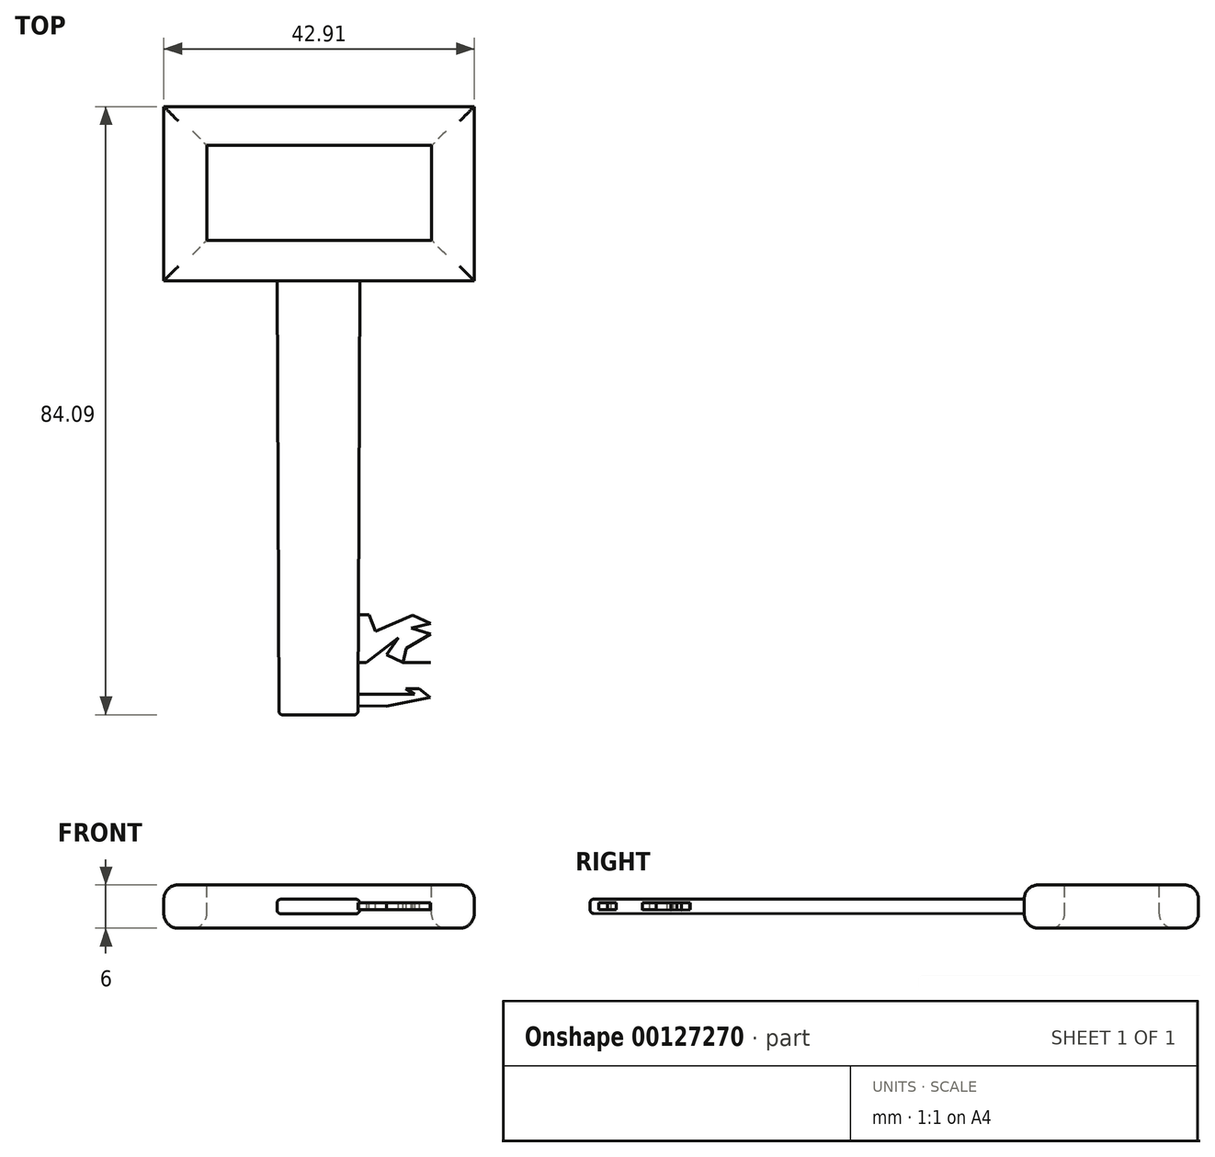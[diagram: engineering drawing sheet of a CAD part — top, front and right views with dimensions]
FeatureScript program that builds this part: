
annotation { "Feature Type Name" : "Feature", "Feature Type Description" : "" }
export const myFeature = defineFeature(function(context is Context, id is Id, definition is map)
    precondition{}
    {
        {
            var Q0;
            Q0=qCreatedBy(makeId("Top.planeOp"),FACE);
            var sketch = newSketch(context, id + "F0", { "sketchPlane" : qUnion([Q0])});
            skLineSegment(sketch, "E0.bottom", {"start": v(-39.45, 64.72) * mm, "end": v(3.46, 64.72) * mm});
            skLineSegment(sketch, "E0.top", {"start": v(-39.45, 40.63) * mm, "end": v(3.46, 40.63) * mm});
            skLineSegment(sketch, "E0.left", {"start": v(-39.45, 64.72) * mm, "end": v(-39.45, 40.63) * mm});
            skLineSegment(sketch, "E0.right", {"start": v(3.46, 64.72) * mm, "end": v(3.46, 40.63) * mm});
            skSolve(sketch);
        }
        {
            var Q0;
            Q0=makeQuery(id+"F0.imprint","IMPRINT",FACE,{"disambiguationData":[TD([[makeQuery(id+"F0.imprint","IMPRINT",EDGE,{"derivedFrom":sQuery(id+"F0.wireOp",EDGE,"E0.bottom")}),-1.0]])]});
            extrude(context, id + "F1", {"entities" : qUnion([Q0]), "depth" : 6 * mm});
        }
        {
            var Q0;
            Q0=makeQuery(id+"F1.opExtrude","CAP_EDGE",EDGE,{"disambiguationData":[OSD([sQuery(id+"F0.wireOp",EDGE,"E0.top")])],"isStart":false});
            var Q1;
            Q1=makeQuery(id+"F1.opExtrude","CAP_EDGE",EDGE,{"disambiguationData":[OSD([sQuery(id+"F0.wireOp",EDGE,"E0.right")])],"isStart":false});
            var Q2;
            Q2=makeQuery(id+"F1.opExtrude","CAP_EDGE",EDGE,{"disambiguationData":[OSD([sQuery(id+"F0.wireOp",EDGE,"E0.bottom")])],"isStart":false});
            var Q3;
            Q3=makeQuery(id+"F1.opExtrude","CAP_EDGE",EDGE,{"disambiguationData":[OSD([sQuery(id+"F0.wireOp",EDGE,"E0.left")])],"isStart":false});
            var Q4;
            Q4=makeQuery(id+"F1.opExtrude","CAP_EDGE",EDGE,{"disambiguationData":[OSD([sQuery(id+"F0.wireOp",EDGE,"E0.top")])],"isStart":true});
            var Q5;
            Q5=makeQuery(id+"F1.opExtrude","CAP_EDGE",EDGE,{"disambiguationData":[OSD([sQuery(id+"F0.wireOp",EDGE,"E0.right")])],"isStart":true});
            var Q6;
            Q6=makeQuery(id+"F1.opExtrude","CAP_EDGE",EDGE,{"disambiguationData":[OSD([sQuery(id+"F0.wireOp",EDGE,"E0.bottom")])],"isStart":true});
            var Q7;
            Q7=makeQuery(id+"F1.opExtrude","CAP_EDGE",EDGE,{"disambiguationData":[OSD([sQuery(id+"F0.wireOp",EDGE,"E0.left")])],"isStart":true});
            fillet(context, id + "F2", {"entities" : qUnion([Q0, Q1, Q2, Q3, Q4, Q5, Q6, Q7]), "radius" : 2 * mm, "tangentPropagation" : true, "allowEdgeOverflow" : false});
        }
        {
            var Q0;
            Q0=makeQuery(id+"F1.opExtrude","CAP_FACE",FACE,{"disambiguationData":[OSD([sQuery(id+"F0.wireOp",EDGE,"E0.bottom"),sQuery(id+"F0.wireOp",EDGE,"E0.top"),sQuery(id+"F0.wireOp",EDGE,"E0.left"),sQuery(id+"F0.wireOp",EDGE,"E0.right")])],"isStart":false});
            var sketch = newSketch(context, id + "F3", { "sketchPlane" : qUnion([Q0])});
            skLineSegment(sketch, "E1.bottom", {"start": v(-33.49, 59.34) * mm, "end": v(-2.43, 59.34) * mm});
            skLineSegment(sketch, "E1.top", {"start": v(-33.49, 46.23) * mm, "end": v(-2.43, 46.23) * mm});
            skLineSegment(sketch, "E1.left", {"start": v(-33.49, 59.34) * mm, "end": v(-33.49, 46.23) * mm});
            skLineSegment(sketch, "E1.right", {"start": v(-2.43, 59.34) * mm, "end": v(-2.43, 46.23) * mm});
            skSolve(sketch);
        }
        {
            var Q0;
            Q0=makeQuery(id+"F3.imprint","IMPRINT",FACE,{"disambiguationData":[TD([[makeQuery(id+"F3.imprint","IMPRINT",EDGE,{"derivedFrom":sQuery(id+"F3.wireOp",EDGE,"E1.bottom")}),-1.0]])]});
            extrude(context, id + "F4", {"entities" : qUnion([Q0]), "operationType" : NewBodyOperationType.REMOVE, "oppositeDirection" : true, "depth" : 30 * mm});
        }
        {
            var Q0;
            Q0=makeQuery(id+"F4.boolean.opBoolean","COPY",EDGE,{"derivedFrom":makeQuery(id+"F4.opExtrude","CAP_EDGE",EDGE,{"disambiguationData":[OSD([sQuery(id+"F3.wireOp",EDGE,"E1.top")])],"isStart":true})});
            var Q1;
            Q1=makeQuery(id+"F4.boolean.opBoolean","COPY",EDGE,{"derivedFrom":makeQuery(id+"F4.opExtrude","CAP_EDGE",EDGE,{"disambiguationData":[OSD([sQuery(id+"F3.wireOp",EDGE,"E1.left")])],"isStart":true})});
            var Q2;
            Q2=makeQuery(id+"F4.boolean.opBoolean","COPY",EDGE,{"derivedFrom":makeQuery(id+"F4.opExtrude","CAP_EDGE",EDGE,{"disambiguationData":[OSD([sQuery(id+"F3.wireOp",EDGE,"E1.bottom")])],"isStart":true})});
            var Q3;
            Q3=makeQuery(id+"F4.boolean.opBoolean","INTERSECT",EDGE,{"derivedFrom":[makeQuery(id+"F1.opExtrude","CAP_FACE",FACE,{"disambiguationData":[OSD([sQuery(id+"F0.wireOp",EDGE,"E0.bottom"),sQuery(id+"F0.wireOp",EDGE,"E0.top"),sQuery(id+"F0.wireOp",EDGE,"E0.left"),sQuery(id+"F0.wireOp",EDGE,"E0.right")])],"isStart":true}),makeQuery(id+"F4.opExtrude","SWEPT_FACE",FACE,{"disambiguationData":[OSD([sQuery(id+"F3.wireOp",EDGE,"E1.left")])]})]});
            var Q4;
            Q4=makeQuery(id+"F4.boolean.opBoolean","INTERSECT",EDGE,{"derivedFrom":[makeQuery(id+"F1.opExtrude","CAP_FACE",FACE,{"disambiguationData":[OSD([sQuery(id+"F0.wireOp",EDGE,"E0.bottom"),sQuery(id+"F0.wireOp",EDGE,"E0.top"),sQuery(id+"F0.wireOp",EDGE,"E0.left"),sQuery(id+"F0.wireOp",EDGE,"E0.right")])],"isStart":true}),makeQuery(id+"F4.opExtrude","SWEPT_FACE",FACE,{"disambiguationData":[OSD([sQuery(id+"F3.wireOp",EDGE,"E1.top")])]})]});
            var Q5;
            Q5=makeQuery(id+"F4.boolean.opBoolean","INTERSECT",EDGE,{"derivedFrom":[makeQuery(id+"F1.opExtrude","CAP_FACE",FACE,{"disambiguationData":[OSD([sQuery(id+"F0.wireOp",EDGE,"E0.bottom"),sQuery(id+"F0.wireOp",EDGE,"E0.top"),sQuery(id+"F0.wireOp",EDGE,"E0.left"),sQuery(id+"F0.wireOp",EDGE,"E0.right")])],"isStart":true}),makeQuery(id+"F4.opExtrude","SWEPT_FACE",FACE,{"disambiguationData":[OSD([sQuery(id+"F3.wireOp",EDGE,"E1.right")])]})]});
            var Q6;
            Q6=makeQuery(id+"F4.boolean.opBoolean","INTERSECT",EDGE,{"derivedFrom":[makeQuery(id+"F1.opExtrude","CAP_FACE",FACE,{"disambiguationData":[OSD([sQuery(id+"F0.wireOp",EDGE,"E0.bottom"),sQuery(id+"F0.wireOp",EDGE,"E0.top"),sQuery(id+"F0.wireOp",EDGE,"E0.left"),sQuery(id+"F0.wireOp",EDGE,"E0.right")])],"isStart":true}),makeQuery(id+"F4.opExtrude","SWEPT_FACE",FACE,{"disambiguationData":[OSD([sQuery(id+"F3.wireOp",EDGE,"E1.bottom")])]})]});
            var Q7;
            Q7=makeQuery(id+"F4.boolean.opBoolean","COPY",EDGE,{"derivedFrom":makeQuery(id+"F4.opExtrude","CAP_EDGE",EDGE,{"disambiguationData":[OSD([sQuery(id+"F3.wireOp",EDGE,"E1.right")])],"isStart":true})});
            fillet(context, id + "F5", {"entities" : qUnion([Q0, Q1, Q2, Q3, Q4, Q5, Q6, Q7]), "radius" : 2 * mm, "tangentPropagation" : true, "allowEdgeOverflow" : false});
        }
        {
            var Q0;
            Q0=makeQuery(id+"F1.opExtrude","SWEPT_FACE",FACE,{"disambiguationData":[OSD([sQuery(id+"F0.wireOp",EDGE,"E0.top")])]});
            cPlane(context, id + "F6", {"entities" : qUnion([Q0]), "cplaneType" : CPlaneType.OFFSET, "offset" : 60 * mm, "width" : 150 * mm, "height" : 150 * mm});
        }
        {
            var Q0;
            Q0=qCreatedBy(id+"F6.planeOp",FACE);
            var sketch = newSketch(context, id + "F7", { "sketchPlane" : qUnion([Q0])});
            skLineSegment(sketch, "E2.bottom", {"start": v(-23.54, 4) * mm, "end": v(-12.62, 4) * mm});
            skLineSegment(sketch, "E2.top", {"start": v(-23.54, 2.06) * mm, "end": v(-12.62, 2.06) * mm});
            skLineSegment(sketch, "E2.left", {"start": v(-23.54, 4) * mm, "end": v(-23.54, 2.06) * mm});
            skLineSegment(sketch, "E2.right", {"start": v(-12.62, 4) * mm, "end": v(-12.62, 2.06) * mm});
            skSolve(sketch);
        }
        {
            var Q0;
            Q0=makeQuery(id+"F1.opExtrude","SWEPT_FACE",FACE,{"disambiguationData":[OSD([sQuery(id+"F0.wireOp",EDGE,"E0.top")])]});
            var sketch = newSketch(context, id + "F8", { "sketchPlane" : qUnion([Q0])});
            skLineSegment(sketch, "E3.bottom", {"start": v(-23.78, 2) * mm, "end": v(-12.38, 2) * mm});
            skLineSegment(sketch, "E3.top", {"start": v(-23.78, 4) * mm, "end": v(-12.38, 4) * mm});
            skLineSegment(sketch, "E3.left", {"start": v(-23.78, 2) * mm, "end": v(-23.78, 4) * mm});
            skLineSegment(sketch, "E3.right", {"start": v(-12.38, 2) * mm, "end": v(-12.38, 4) * mm});
            skSolve(sketch);
        }
        {
            var Q1;
            Q1=makeQuery(id+"F7.imprint","IMPRINT",FACE,{"disambiguationData":[TD([[makeQuery(id+"F7.imprint","IMPRINT",EDGE,{"derivedFrom":sQuery(id+"F7.wireOp",EDGE,"E2.bottom")}),-1.0]])]});
            var Q2;
            Q2=makeQuery(id+"F8.imprint","IMPRINT",FACE,{"disambiguationData":[TD([[makeQuery(id+"F8.imprint","IMPRINT",EDGE,{"derivedFrom":sQuery(id+"F8.wireOp",EDGE,"E3.bottom")}),1.0]])]});
            loft(context, id + "F9", {"operationType" : NewBodyOperationType.ADD, "sheetProfilesArray" : [{ "sheetProfileEntities" : qUnion([Q1]) }, { "sheetProfileEntities" : qUnion([Q2]) }]});
        }
        {
            var Q0;
            Q0=makeQuery(id+"F9.opLoft","SWEPT_EDGE",EDGE,{"disambiguationData":[OSD([sQuery(id+"F0.wireOp",EDGE,"E0.top"),sQuery(id+"F7.wireOp",EDGE,"E2.bottom"),sQuery(id+"F7.wireOp",EDGE,"E2.left"),sQuery(id+"F8.wireOp",EDGE,"E3.top"),sQuery(id+"F8.wireOp",EDGE,"E3.left")])]});
            var Q1;
            Q1=makeQuery(id+"F9.opLoft","SWEPT_EDGE",EDGE,{"disambiguationData":[OSD([sQuery(id+"F0.wireOp",EDGE,"E0.top"),sQuery(id+"F7.wireOp",EDGE,"E2.top"),sQuery(id+"F7.wireOp",EDGE,"E2.left"),sQuery(id+"F8.wireOp",EDGE,"E3.bottom"),sQuery(id+"F8.wireOp",EDGE,"E3.left")])]});
            var Q2;
            Q2=makeQuery(id+"F9.opLoft","MID_CAP_EDGE",EDGE,{"disambiguationData":[OSD([sQuery(id+"F7.wireOp",EDGE,"E2.top"),sQuery(id+"F7.wireOp",EDGE,"E2.left"),sQuery(id+"F7.wireOp",EDGE,"E2.right")])],"capPos":0.0});
            var Q3;
            Q3=makeQuery(id+"F9.opLoft","MID_CAP_EDGE",EDGE,{"disambiguationData":[OSD([sQuery(id+"F7.wireOp",EDGE,"E2.bottom"),sQuery(id+"F7.wireOp",EDGE,"E2.left"),sQuery(id+"F7.wireOp",EDGE,"E2.right")])],"capPos":0.0});
            var Q4;
            Q4=makeQuery(id+"F9.opLoft","SWEPT_EDGE",EDGE,{"disambiguationData":[OSD([sQuery(id+"F0.wireOp",EDGE,"E0.top"),sQuery(id+"F7.wireOp",EDGE,"E2.bottom"),sQuery(id+"F7.wireOp",EDGE,"E2.right"),sQuery(id+"F8.wireOp",EDGE,"E3.top"),sQuery(id+"F8.wireOp",EDGE,"E3.right")])]});
            var Q5;
            Q5=makeQuery(id+"F9.opLoft","MID_CAP_EDGE",EDGE,{"disambiguationData":[OSD([sQuery(id+"F7.wireOp",EDGE,"E2.bottom"),sQuery(id+"F7.wireOp",EDGE,"E2.top"),sQuery(id+"F7.wireOp",EDGE,"E2.right")])],"capPos":0.0});
            var Q6;
            Q6=makeQuery(id+"F9.opLoft","MID_CAP_EDGE",EDGE,{"disambiguationData":[OSD([sQuery(id+"F7.wireOp",EDGE,"E2.bottom"),sQuery(id+"F7.wireOp",EDGE,"E2.top"),sQuery(id+"F7.wireOp",EDGE,"E2.left")])],"capPos":0.0});
            var Q7;
            Q7=makeQuery(id+"F9.opLoft","SWEPT_EDGE",EDGE,{"disambiguationData":[OSD([sQuery(id+"F0.wireOp",EDGE,"E0.top"),sQuery(id+"F7.wireOp",EDGE,"E2.top"),sQuery(id+"F7.wireOp",EDGE,"E2.right"),sQuery(id+"F8.wireOp",EDGE,"E3.bottom"),sQuery(id+"F8.wireOp",EDGE,"E3.right")])]});
            fillet(context, id + "F10", {"entities" : qUnion([Q0, Q1, Q2, Q3, Q4, Q5, Q6, Q7]), "radius" : 0.5 * mm, "tangentPropagation" : true, "allowEdgeOverflow" : false});
        }
        {
            var Q0;
            Q0=makeQuery(id+"F9.opLoft","SWEPT_FACE",FACE,{"disambiguationData":[OSD([sQuery(id+"F0.wireOp",EDGE,"E0.top"),sQuery(id+"F7.wireOp",EDGE,"E2.bottom"),sQuery(id+"F7.wireOp",EDGE,"E2.top"),sQuery(id+"F7.wireOp",EDGE,"E2.right"),sQuery(id+"F8.wireOp",EDGE,"E3.bottom"),sQuery(id+"F8.wireOp",EDGE,"E3.top"),sQuery(id+"F8.wireOp",EDGE,"E3.right")])]});
            cPlane(context, id + "F11", {"entities" : qUnion([Q0]), "cplaneType" : CPlaneType.OFFSET, "offset" : 10 * mm, "width" : 150 * mm, "height" : 150 * mm});
        }
        {
            var Q0;
            Q0=qCreatedBy(id+"F11.planeOp",FACE);
            var sketch = newSketch(context, id + "F12", { "sketchPlane" : qUnion([Q0])});
            skLineSegment(sketch, "E4.bottom", {"start": v(-12.16, 3.53) * mm, "end": v(-5.61, 3.53) * mm});
            skLineSegment(sketch, "E4.top", {"start": v(-12.16, 2.53) * mm, "end": v(-5.61, 2.53) * mm});
            skLineSegment(sketch, "E4.left", {"start": v(-12.16, 3.53) * mm, "end": v(-12.16, 2.53) * mm});
            skLineSegment(sketch, "E4.right", {"start": v(-5.61, 3.53) * mm, "end": v(-5.61, 2.53) * mm});
            skSolve(sketch);
        }
        {
            var Q0;
            Q0=makeQuery(id+"F9.opLoft","SWEPT_FACE",FACE,{"disambiguationData":[OSD([sQuery(id+"F0.wireOp",EDGE,"E0.top"),sQuery(id+"F7.wireOp",EDGE,"E2.bottom"),sQuery(id+"F7.wireOp",EDGE,"E2.top"),sQuery(id+"F7.wireOp",EDGE,"E2.right"),sQuery(id+"F8.wireOp",EDGE,"E3.bottom"),sQuery(id+"F8.wireOp",EDGE,"E3.top"),sQuery(id+"F8.wireOp",EDGE,"E3.right")])]});
            var sketch = newSketch(context, id + "F13", { "sketchPlane" : qUnion([Q0])});
            skLineSegment(sketch, "E5.bottom", {"start": v(-12.2, 2.56) * mm, "end": v(-5.59, 2.56) * mm});
            skLineSegment(sketch, "E5.top", {"start": v(-12.2, 3.5) * mm, "end": v(-5.59, 3.5) * mm});
            skLineSegment(sketch, "E5.left", {"start": v(-12.2, 2.56) * mm, "end": v(-12.2, 3.5) * mm});
            skLineSegment(sketch, "E5.right", {"start": v(-5.59, 2.56) * mm, "end": v(-5.59, 3.5) * mm});
            skSolve(sketch);
        }
        {
            var Q1;
            Q1=makeQuery(id+"F12.imprint","IMPRINT",FACE,{"disambiguationData":[TD([[makeQuery(id+"F12.imprint","IMPRINT",EDGE,{"derivedFrom":sQuery(id+"F12.wireOp",EDGE,"E4.bottom")}),-1.0]])]});
            var Q2;
            Q2=makeQuery(id+"F13.imprint","IMPRINT",FACE,{"disambiguationData":[TD([[makeQuery(id+"F13.imprint","IMPRINT",EDGE,{"derivedFrom":sQuery(id+"F13.wireOp",EDGE,"E5.bottom")}),1.0]])]});
            loft(context, id + "F14", {"operationType" : NewBodyOperationType.ADD, "sheetProfilesArray" : [{ "sheetProfileEntities" : qUnion([Q1]) }, { "sheetProfileEntities" : qUnion([Q2]) }]});
        }
        {
            var Q0;
            Q0=makeQuery(id+"F14.opLoft","SWEPT_FACE",FACE,{"disambiguationData":[OSD([sQuery(id+"F0.wireOp",EDGE,"E0.top"),sQuery(id+"F7.wireOp",EDGE,"E2.bottom"),sQuery(id+"F7.wireOp",EDGE,"E2.top"),sQuery(id+"F7.wireOp",EDGE,"E2.right"),sQuery(id+"F8.wireOp",EDGE,"E3.bottom"),sQuery(id+"F8.wireOp",EDGE,"E3.top"),sQuery(id+"F8.wireOp",EDGE,"E3.right"),sQuery(id+"F12.wireOp",EDGE,"E4.bottom"),sQuery(id+"F12.wireOp",EDGE,"E4.left"),sQuery(id+"F12.wireOp",EDGE,"E4.right"),sQuery(id+"F13.wireOp",EDGE,"E5.top"),sQuery(id+"F13.wireOp",EDGE,"E5.left"),sQuery(id+"F13.wireOp",EDGE,"E5.right")])]});
            var sketch = newSketch(context, id + "F15", { "sketchPlane" : qUnion([Q0])});
            skLineSegment(sketch, "E6", {"start": v(-11.45, -12.16) * mm, "end": v(-7.02, -8.7) * mm});
            skLineSegment(sketch, "E7", {"start": v(-7.02, -8.7) * mm, "end": v(-8.63, -11.08) * mm});
            skLineSegment(sketch, "E8", {"start": v(-8.63, -11.08) * mm, "end": v(-6.36, -12.15) * mm});
            skLineSegment(sketch, "E9", {"start": v(-6.36, -12.15) * mm, "end": v(-2.57, -10.2) * mm});
            skLineSegment(sketch, "E10", {"start": v(-2.57, -10.2) * mm, "end": v(-5.9, -10.2) * mm});
            skLineSegment(sketch, "E11", {"start": v(-5.9, -10.2) * mm, "end": v(-2.56, -8.22) * mm});
            skLineSegment(sketch, "E12", {"start": v(-2.56, -8.22) * mm, "end": v(-3.68, -10.2) * mm});
            skLineSegment(sketch, "E13", {"start": v(-5.9, -10.2) * mm, "end": v(-6.36, -12.15) * mm});
            skLineSegment(sketch, "E14", {"start": v(-5.9, -10.2) * mm, "end": v(-8.63, -11.08) * mm});
            skLineSegment(sketch, "E15", {"start": v(-2.57, -10.2) * mm, "end": v(-2.58, -12.15) * mm});
            skLineSegment(sketch, "E16", {"start": v(-6.36, -12.13) * mm, "end": v(-2.58, -12.15) * mm});
            skLineSegment(sketch, "E17", {"start": v(-6.36, -12.15) * mm, "end": v(-2.58, -12.15) * mm});
            skLineSegment(sketch, "E18", {"start": v(-11.09, -5.55) * mm, "end": v(-10.18, -7.83) * mm});
            skLineSegment(sketch, "E19", {"start": v(-10.18, -7.83) * mm, "end": v(-5.06, -5.59) * mm});
            skLineSegment(sketch, "E20", {"start": v(-5.06, -5.59) * mm, "end": v(-2.56, -6.74) * mm});
            skLineSegment(sketch, "E21", {"start": v(-2.56, -6.74) * mm, "end": v(-5.2, -7.36) * mm});
            skLineSegment(sketch, "E22", {"start": v(-5.2, -7.36) * mm, "end": v(-10.18, -7.83) * mm});
            skLineSegment(sketch, "E23", {"start": v(-5.2, -7.36) * mm, "end": v(-2.56, -8.22) * mm});
            skLineSegment(sketch, "E24", {"start": v(-6.36, -12.15) * mm, "end": v(-2.58, -12.37) * mm});
            skLineSegment(sketch, "E25", {"start": v(-2.58, -12.37) * mm, "end": v(-2.58, -12.15) * mm});
            skSolve(sketch);
        }
        {
            var Q0;
            {var subQ0=sQuery(id+"F15.wireOp",EDGE,"E18");Q0=makeQuery(id+"F15.imprint","IMPRINT",FACE,{"disambiguationData":[TD([[makeQuery(id+"F15.imprint","IMPRINT",EDGE,{"derivedFrom":subQ0}),1.0]])]});}
            var Q1;
            {var subQ0=sQuery(id+"F15.wireOp",EDGE,"E20");Q1=makeQuery(id+"F15.imprint","IMPRINT",FACE,{"disambiguationData":[TD([[makeQuery(id+"F15.imprint","IMPRINT",EDGE,{"derivedFrom":subQ0}),1.0]])]});}
            var Q2;
            {var subQ0=sQuery(id+"F15.wireOp",EDGE,"E21");Q2=makeQuery(id+"F15.imprint","IMPRINT",FACE,{"disambiguationData":[TD([[makeQuery(id+"F15.imprint","IMPRINT",EDGE,{"derivedFrom":subQ0}),1.0]])]});}
            var Q3;
            {var subQ3=sQuery(id+"F15.wireOp",EDGE,"E12");Q3=makeQuery(id+"F15.imprint","IMPRINT",FACE,{"disambiguationData":[TD([[makeQuery(id+"F15.imprint","IMPRINT",EDGE,{"derivedFrom":subQ3}),1.0]])]});}
            var Q4;
            {var subQ0=sQuery(id+"F15.wireOp",EDGE,"E13");var subQ3=sQuery(id+"F15.wireOp",EDGE,"E16");var subQ4=makeQuery(id+"F15.imprint","INTERSECT",VERTEX,{"derivedFrom":[subQ0,subQ3]});Q4=makeQuery(id+"F15.imprint","IMPRINT",FACE,{"disambiguationData":[TD([[makeQuery(id+"F15.imprint","IMPRINT",EDGE,{"disambiguationData":[TD([[subQ4,-1.0]])],"derivedFrom":subQ3}),1.0]])]});}
            var Q5;
            {var subQ0=sQuery(id+"F15.wireOp",EDGE,"E6");Q5=makeQuery(id+"F15.imprint","IMPRINT",FACE,{"disambiguationData":[TD([[makeQuery(id+"F15.imprint","IMPRINT",EDGE,{"derivedFrom":subQ0}),-1.0]])]});}
            var Q6;
            {var subQ0=sQuery(id+"F15.wireOp",EDGE,"E11");Q6=makeQuery(id+"F15.imprint","IMPRINT",FACE,{"disambiguationData":[TD([[makeQuery(id+"F15.imprint","IMPRINT",EDGE,{"derivedFrom":subQ0}),-1.0]])]});}
            var Q7;
            Q7=makeQuery(id+"F15.imprint","IMPRINT",FACE,{"disambiguationData":[TD([[makeQuery(id+"F15.imprint","IMPRINT",EDGE,{"derivedFrom":sQuery(id+"F15.wireOp",EDGE,"E17")}),1.0]])]});
            var Q8;
            {var subQ0=sQuery(id+"F15.wireOp",EDGE,"E15");Q8=makeQuery(id+"F15.imprint","IMPRINT",FACE,{"disambiguationData":[TD([[makeQuery(id+"F15.imprint","IMPRINT",EDGE,{"derivedFrom":subQ0}),1.0]])]});}
            extrude(context, id + "F16", {"entities" : qUnion([Q0, Q1, Q2, Q3, Q4, Q5, Q6, Q7, Q8]), "operationType" : NewBodyOperationType.REMOVE, "oppositeDirection" : true, "depth" : 25 * mm});
        }
        {
            var Q0;
            {var subQ0=sQuery(id+"F7.wireOp",EDGE,"E2.right");var subQ1=sQuery(id+"F7.wireOp",EDGE,"E2.top");var subQ2=sQuery(id+"F7.wireOp",EDGE,"E2.bottom");var subQ9=sQuery(id+"F8.wireOp",EDGE,"E3.right");var subQ10=sQuery(id+"F8.wireOp",EDGE,"E3.top");var subQ11=sQuery(id+"F8.wireOp",EDGE,"E3.bottom");var subQ12=sQuery(id+"F0.wireOp",EDGE,"E0.top");var subQ13=makeQuery(id+"F9.opLoft","SWEPT_FACE",FACE,{"disambiguationData":[OSD([subQ12,subQ2,subQ1,subQ0,subQ11,subQ10,subQ9])]});Q0=makeQuery(id+"F14.boolean.opBoolean","SPLIT",FACE,{"disambiguationData":[TD([makeQuery(id+"F10.opFillet","BLEND_FACE",FACE,{"disambiguationData":[OSD([subQ2,subQ0])]})])],"derivedFrom":subQ13});}
            var sketch = newSketch(context, id + "F17", { "sketchPlane" : qUnion([Q0])});
            skLineSegment(sketch, "E26.bottom", {"start": v(-18.19, 2.56) * mm, "end": v(-15.78, 2.56) * mm});
            skLineSegment(sketch, "E26.top", {"start": v(-18.19, 3.5) * mm, "end": v(-15.78, 3.5) * mm});
            skLineSegment(sketch, "E26.left", {"start": v(-18.19, 2.56) * mm, "end": v(-18.19, 3.5) * mm});
            skLineSegment(sketch, "E26.right", {"start": v(-15.78, 2.56) * mm, "end": v(-15.78, 3.5) * mm});
            skSolve(sketch);
        }
        {
            var Q0;
            Q0=makeQuery(id+"F17.imprint","IMPRINT",FACE,{"disambiguationData":[TD([[makeQuery(id+"F17.imprint","IMPRINT",EDGE,{"derivedFrom":sQuery(id+"F17.wireOp",EDGE,"E26.bottom")}),1.0]])]});
            extrude(context, id + "F18", {"entities" : qUnion([Q0]), "operationType" : NewBodyOperationType.ADD, "depth" : 10 * mm});
        }
        {
            var Q0;
            Q0=makeQuery(id+"F18.opExtrude","SWEPT_FACE",FACE,{"disambiguationData":[OSD([sQuery(id+"F17.wireOp",EDGE,"E26.bottom")])]});
            var sketch = newSketch(context, id + "F19", { "sketchPlane" : qUnion([Q0])});
            skLineSegment(sketch, "E27", {"start": v(-8.69, 18.15) * mm, "end": v(-2.6, 16.97) * mm});
            skLineSegment(sketch, "E28", {"start": v(-2.6, 16.97) * mm, "end": v(-4.15, 15.77) * mm});
            skLineSegment(sketch, "E29", {"start": v(-5.98, 15.76) * mm, "end": v(-4.8, 16.54) * mm});
            skLineSegment(sketch, "E30", {"start": v(-4.8, 16.54) * mm, "end": v(-12.6, 16.54) * mm});
            skSolve(sketch);
        }
        {
            var Q0;
            {var subQ0=sQuery(id+"F19.wireOp",EDGE,"E27");Q0=makeQuery(id+"F19.imprint","IMPRINT",FACE,{"disambiguationData":[TD([[makeQuery(id+"F19.imprint","IMPRINT",EDGE,{"derivedFrom":subQ0}),1.0]])]});}
            var Q1;
            {var subQ0=sQuery(id+"F19.wireOp",EDGE,"E28");Q1=makeQuery(id+"F19.imprint","IMPRINT",FACE,{"disambiguationData":[TD([[makeQuery(id+"F19.imprint","IMPRINT",EDGE,{"derivedFrom":subQ0}),1.0]])]});}
            var Q2;
            {var subQ0=sQuery(id+"F19.wireOp",EDGE,"E29");Q2=makeQuery(id+"F19.imprint","IMPRINT",FACE,{"disambiguationData":[TD([[makeQuery(id+"F19.imprint","IMPRINT",EDGE,{"derivedFrom":subQ0}),1.0]])]});}
            extrude(context, id + "F20", {"entities" : qUnion([Q0, Q1, Q2]), "operationType" : NewBodyOperationType.REMOVE, "oppositeDirection" : true, "depth" : 25 * mm});
        }
    });
